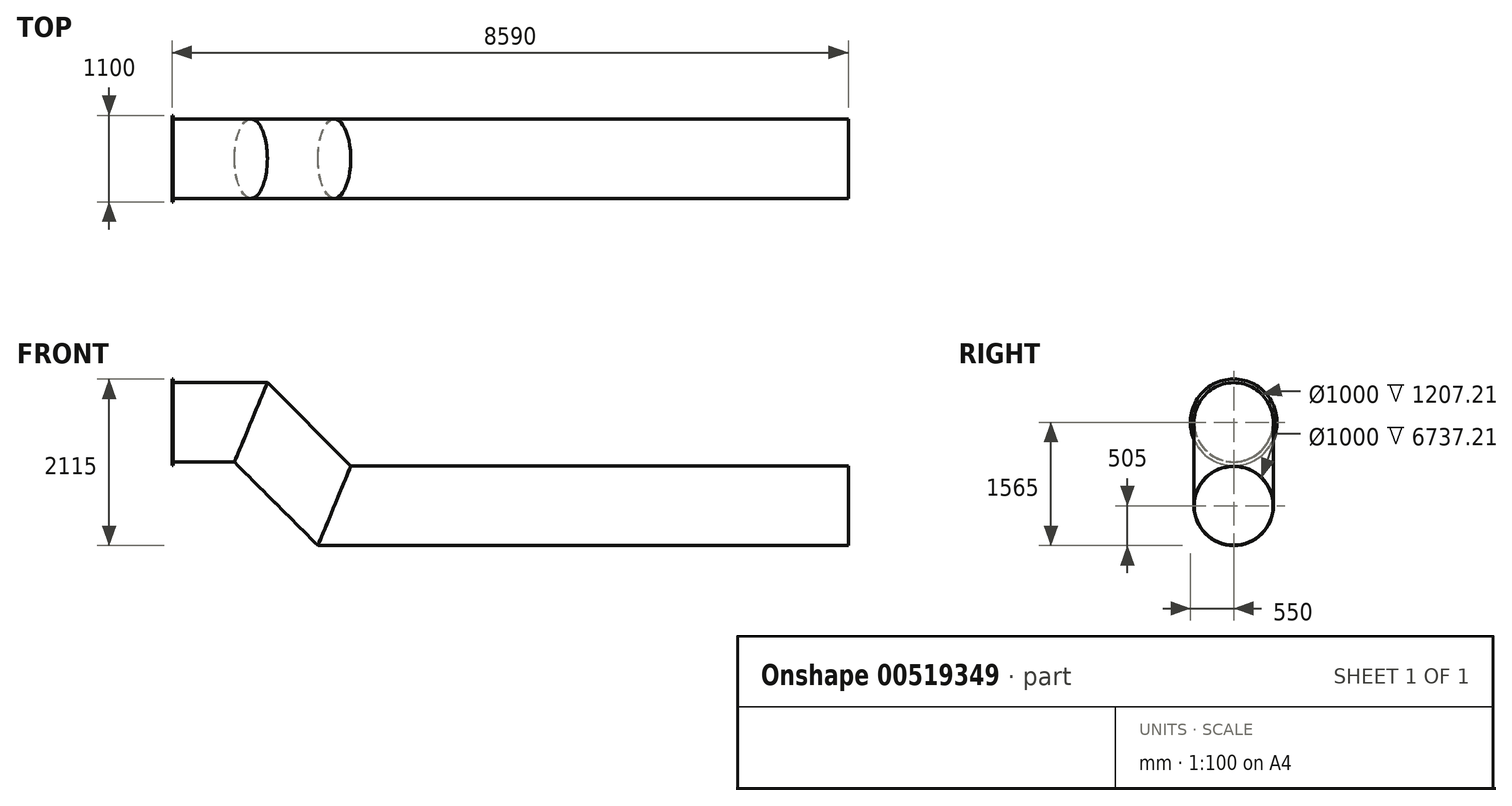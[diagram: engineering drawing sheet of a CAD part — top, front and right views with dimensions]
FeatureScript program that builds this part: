
annotation { "Feature Type Name" : "Feature", "Feature Type Description" : "" }
export const myFeature = defineFeature(function(context is Context, id is Id, definition is map)
    precondition{}
    {
        {
            var Q0;
            Q0=qCreatedBy(makeId("Front.planeOp"),FACE);
            var sketch = newSketch(context, id + "F0", { "sketchPlane" : qUnion([Q0])});
            skLineSegment(sketch, "E0", {"start": v(0, 0) * mm, "end": v(1000, 0) * mm});
            skLineSegment(sketch, "E1", {"start": v(1000, 0) * mm, "end": v(2060, -1060) * mm});
            skLineSegment(sketch, "E2", {"start": v(2060, -1060) * mm, "end": v(8590, -1060) * mm});
            skSolve(sketch);
        }
        {
            var Q0;
            Q0=qCreatedBy(makeId("Right.planeOp"),FACE);
            var sketch = newSketch(context, id + "F1", { "sketchPlane" : qUnion([Q0])});
            skCircle(sketch, "E3", {"center": v(0, 0) * mm, "radius": 500 * mm});
            skCircle(sketch, "E4", {"center": v(0, 0) * mm, "radius": 505 * mm});
            skSolve(sketch);
        }
        {
            var Q0;
            Q0 = qSketchRegion(id + "F1", true);
            var Q1;
            Q1 = qConstructionFilter(qBodyType(qCreatedBy(id + "F0" ,EDGE), BodyType.WIRE), ConstructionObject.NO);
            sweep(context, id + "F2", {"profiles" : qUnion([Q0]), "path" : qUnion([Q1])});
        }
        {
            var Q0;
            Q0=makeQuery(id+"F2.opSweep","CAP_FACE",FACE,{"disambiguationData":[OSD([sQuery(id+"F0.wireOp",VERTEX,"E0.start"),sQuery(id+"F1.wireOp",EDGE,"E3"),sQuery(id+"F1.wireOp",EDGE,"E4")])],"isStart":true});
            var sketch = newSketch(context, id + "F3", { "sketchPlane" : qUnion([Q0])});
            skCircle(sketch, "E5.0", {"center": v(0, 0) * mm, "radius": 500 * mm});
            skCircle(sketch, "E6", {"center": v(0, 0) * mm, "radius": 550 * mm});
            skSolve(sketch);
        }
        {
            var Q0;
            Q0 = qSketchRegion(id + "F3", true);
            extrude(context, id + "F4", {"entities" : qUnion([Q0]), "operationType" : NewBodyOperationType.ADD, "oppositeDirection" : true, "depth" : 10 * mm, "offsetDistance" : 25 * mm});
        }
    });
